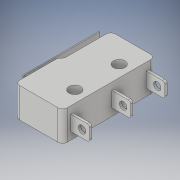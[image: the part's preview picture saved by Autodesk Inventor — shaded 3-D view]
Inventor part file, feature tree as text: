
AUTODESK INVENTOR PART (.ipt)
format: ipt  version: 2019 (Build 230136000, 136)  size: 213,504 bytes
history: native  units: mm
features: extrude x4, sketch x4, fillet x2
ambient origin geometry x8: Origin, YZ Plane, XZ Plane, XY Plane, X Axis, Y Axis, Z Axis, Center Point
bodies: Solid1 (feature_tree)
feature tree (10):
  extrude  "Extrusion1"  Depth=19.8mm
  extrude  "Extrusion2"  Depth=2.5mm
  extrude  "Extrusion3"  TaperAngle=0.0deg  [1 undecoded]
  extrude  "Extrusion4"  Depth=9.5mm
  fillet  "Fillet1"  [1 undecoded]
  fillet  "Fillet2"  Radius=2.5mm
  sketch  "Sketch1"  dims[d0=10.2mm d1=19.8mm]
  sketch  "Sketch2"  dims[d3=90.0deg d4=2.5mm]
  sketch  "Sketch3"  dims[d5=5.1mm d6=0.0mm]
  sketch  "Sketch4"  dims[d7=2.5mm d8=9.5mm d9=90.0deg d10=2.5mm d11=9.5mm d12=0.0mm d13=135.0deg d14=3.075914mm d15=6.4mm d16=0.0mm d17=2.8mm d18=90.0deg d19=1.9mm d20=0.0mm d21=2.0mm d22=2.0mm d23=0.2mm d24=90.0deg d25=0.2mm d26=3.8mm d27=0.0mm d28=2.0mm d29=8.8mm d30=7.3mm d31=8.0mm d32=0.5mm d33=8.0mm d34=0.5mm d35=8.0mm d36=0.5mm d37=3.2mm d38=0.0mm d39=3.2mm d40=1.6mm d41=40.0mm d42=0.0mm d43=1.0mm d44=0.5mm]
note: 2 required parameter values undecoded (feature->parameter linkage not recoverable at this tier; creation-order binding heuristic only, values carry confidence <= 0.55)
